# Revit family: Haworth_UniGroupToo_DShapedConvergent
name_source: partatom
category: Furniture Systems
revit_build: Autodesk Revit 2018 (Build: 20170223_1515(x64)
units: mm (PartAtom-declared; Revit-internal decimal feet)

## family parameters
Always vertical = Yes
Cut with Voids When Loaded = No
OmniClass Number = 23.40.70.14.64.21.21
OmniClass Title = Desk System
Part Type = Normal
Room Calculation Point = No
Round Connector Dimension = Use Diameter
Shared = No
Work Plane-Based = No

## types (1)
- 30w 72L
    Actual Height = 29"
    Actual Length = 72"
    Actual Width = 30"
    Assembly Code = E2020200
    Custom Size = No
    Deep Worksurface Thickness = No
    Description = Haworth - UniGroupToo - D Shaped Convergent
    End Support Location = 1 3/4"
    Height = 29"
    Leg Location = 15"
    Length = 72"
    Manufacturer = Haworth
    Max. Depth = 36"
    Max. Height = 42"
    Max. Width = 72"
    Min. Depth = 18"
    Min. Height = 26"
    Min. Width = 36"
    Model = Haworth - UniGroupToo - D Shaped Convergent
    Radius = 15"
    Revision Number = 2
    Size = Verify Final Dim. w/ Haworth
    Standard Length = 36-72 in. @ 6 in. increments
    Standard Widths = 18,24,30 in.
    Standard Worksurface Thickness = Yes
    Support Column = Yes
    Support Finish = Haworth _ Paint _ Metallic Champagne
    Support Height = 27 13/16"
    Sustainability Info = http://www.haworth.com
    Top Thickness = 1 3/16"
    URL = www.haworth.com
    URL - Product = http://www.haworth.com
    Warranty = http://www.haworth.com
    Width = 30"
    Worksurface Edge Finish = Haworth _ Wood _ White Oak
    Worksurface Finish = Haworth _ Wood _ White Oak

## geometry (parser evidence)
native form markers: Sweep x8
no freeform markers — native parametric forms only
